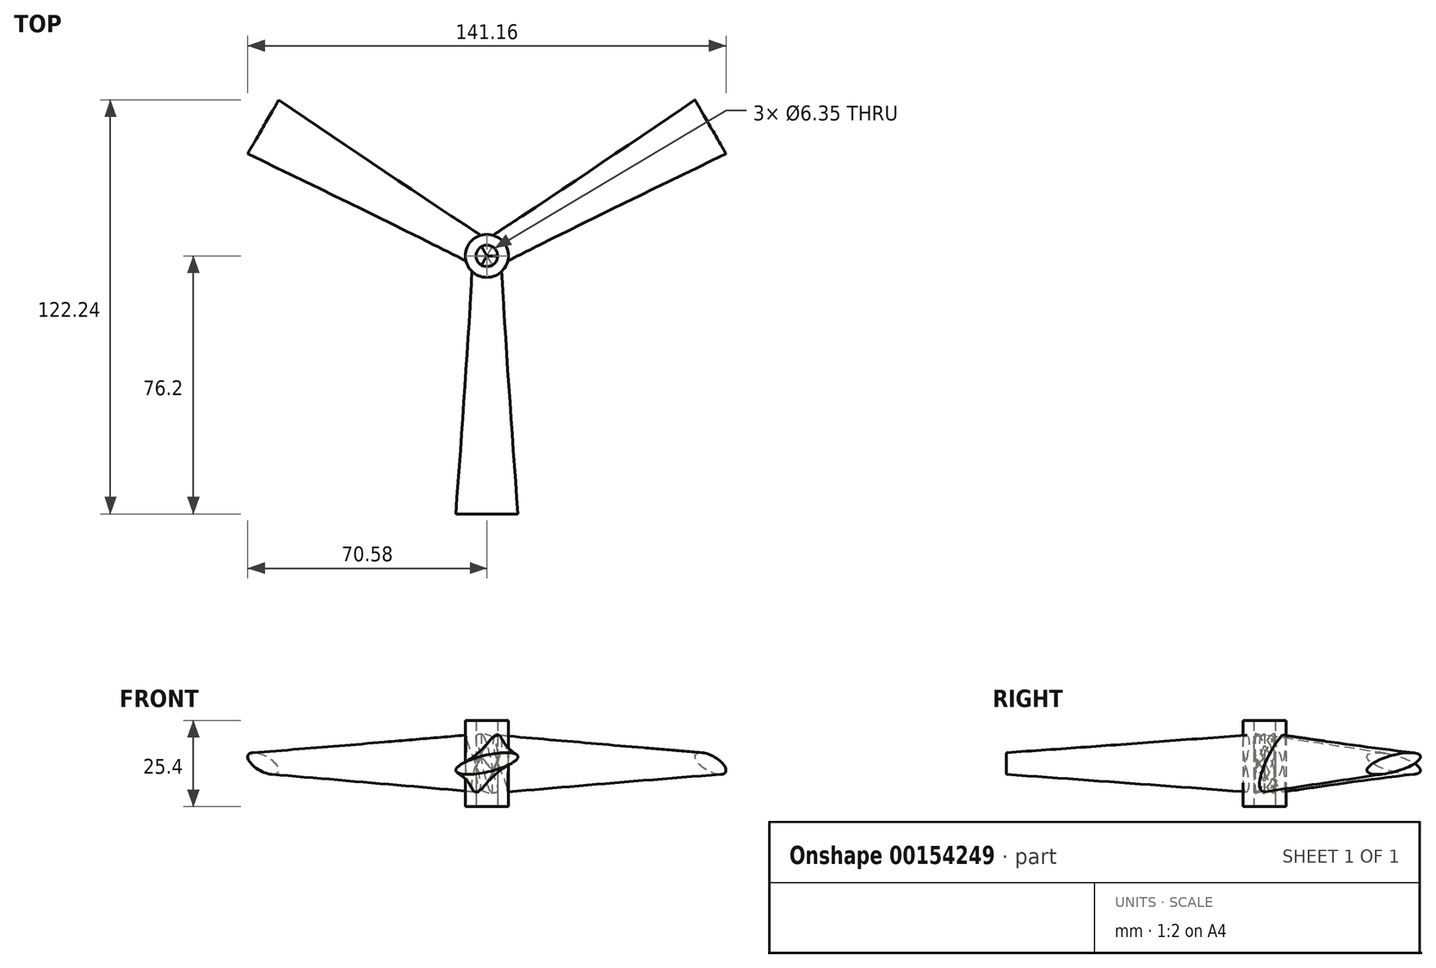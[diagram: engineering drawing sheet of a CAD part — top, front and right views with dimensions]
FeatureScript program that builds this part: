
annotation { "Feature Type Name" : "Feature", "Feature Type Description" : "" }
export const myFeature = defineFeature(function(context is Context, id is Id, definition is map)
    precondition{}
    {
        {
            var Q0;
            Q0=qCreatedBy(makeId("Top.planeOp"),FACE);
            var sketch = newSketch(context, id + "F0", { "sketchPlane" : qUnion([Q0])});
            skCircle(sketch, "E0", {"center": v(0, 0) * mm, "radius": 6.35 * mm});
            skCircle(sketch, "E1", {"center": v(0, 0) * mm, "radius": 3.18 * mm});
            skSolve(sketch);
        }
        {
            var Q0;
            Q0 = qSketchRegion(id + "F0", true);
            extrude(context, id + "F1", {"entities" : qUnion([Q0]), "depth" : 25.4 * mm});
        }
        {
            var Q0;
            Q0=qCreatedBy(makeId("Front.planeOp"),FACE);
            var sketch = newSketch(context, id + "F2", { "sketchPlane" : qUnion([Q0])});
            skLineSegment(sketch, "E2", {"start": v(0, 0) * mm, "end": v(0, 12.7) * mm});
            skEllipse(sketch, "E3", {"center": v(0, 12.7) * mm, "majorRadius": 9.4 * mm, "minorRadius": 2.46 * mm, "majorAxis": v(0.37, 0.93)});
            skSolve(sketch);
        }
        {
            var Q0;
            Q0=qCreatedBy(makeId("Front.planeOp"),FACE);
            cPlane(context, id + "F3", {"entities" : qUnion([Q0]), "cplaneType" : CPlaneType.OFFSET, "offset" : 76.2 * mm, "width" : 152.4 * mm, "height" : 152.4 * mm});
        }
        {
            var Q0;
            Q0=qCreatedBy(id+"F3.planeOp",FACE);
            var sketch = newSketch(context, id + "F4", { "sketchPlane" : qUnion([Q0])});
            skEllipse(sketch, "E4.0", {"center": v(0, 12.7) * mm, "majorRadius": 9.4 * mm, "minorRadius": 2.46 * mm, "majorAxis": v(0.97, 0.23)});
            skSolve(sketch);
        }
        {
            var Q1;
            Q1=makeQuery(id+"F2.imprint","IMPRINT",FACE,{"disambiguationData":[TD([[makeQuery(id+"F2.imprint","IMPRINT",EDGE,{"derivedFrom":sQuery(id+"F2.wireOp",EDGE,"E3")}),1.0]])]});
            var Q2;
            Q2=makeQuery(id+"F4.imprint","IMPRINT",FACE,{"disambiguationData":[TD([[makeQuery(id+"F4.imprint","IMPRINT",EDGE,{"derivedFrom":sQuery(id+"F4.wireOp",EDGE,"E4.0")}),1.0]])]});
            loft(context, id + "F5", {"operationType" : NewBodyOperationType.ADD, "sheetProfilesArray" : [{ "sheetProfileEntities" : qUnion([Q1]) }, { "sheetProfileEntities" : qUnion([Q2]) }]});
        }
        {
            var Q0;
            Q0=qCreatedBy(makeId("Front.planeOp"),FACE);
            var sketch = newSketch(context, id + "F6", { "sketchPlane" : qUnion([Q0])});
            skLineSegment(sketch, "E5", {"start": v(0, 0) * mm, "end": v(0, 48.95) * mm, "construction": true});
            skSolve(sketch);
        }
        {
            var Q0;
            Q0=makeQuery(id+"F1.opExtrude","SWEPT_BODY",BODY,{"disambiguationData":[OSD([sQuery(id+"F0.wireOp",EDGE,"E0"),sQuery(id+"F0.wireOp",EDGE,"E1")])]});
            var Q1;
            Q1=sQuery(id+"F6.wireOp",EDGE,"E5");
            circularPattern(context, id + "F7", {"entities" : qUnion([Q0]), "axis" : qUnion([Q1]), "angle" : 360 * degree, "instanceCount" : 3, "equalSpace" : true});
        }
    });
